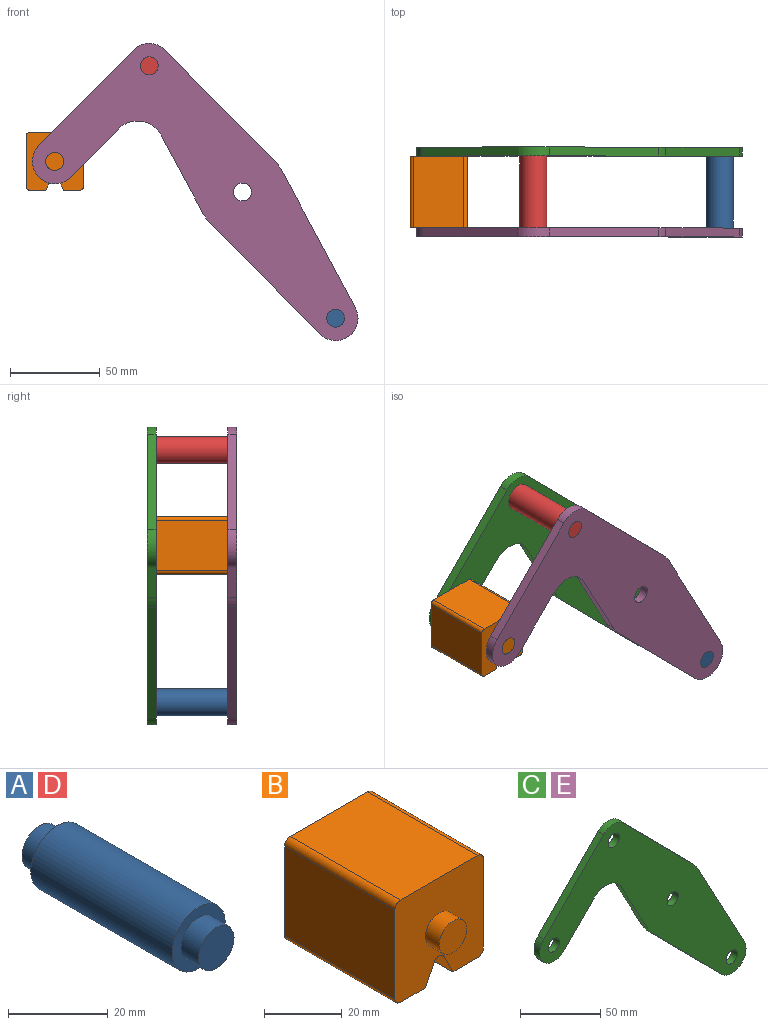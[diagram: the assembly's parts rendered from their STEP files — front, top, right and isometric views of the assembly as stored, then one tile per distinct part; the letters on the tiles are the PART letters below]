
ASSEMBLY  parts=5 mates=3
PART A: 7 faces, bbox 15x50x15 mm
  f0: cylinder r=7.5mm len=40mm, axis (0,-1,0), area 1885mm2, adj f2,f5
  f1: cylinder r=5mm len=10mm, axis (0,1,0), area 157.1mm2, adj f2,f3
  f2: plane 15x15mm, normal (0,-1,0), area 98.2mm2, adj f0,f1
  f3: plane 10x10mm, normal (0,-1,0), area 78.5mm2, adj f1
  f4: cylinder r=5mm len=10mm, axis (0,-1,0), area 157.1mm2, adj f5,f6
  f5: plane 15x15mm, normal (0,1,0), area 98.2mm2, adj f0,f4
  f6: plane 10x10mm, normal (0,1,0), area 78.5mm2, adj f4
PART B: 18 faces, bbox 32.1x50x32.1 mm
  f0: plane 40x28.08mm, normal (1,0,0), area 1123.1mm2, adj f4,f10,f13,f14
  f1: plane 40x9.04mm, normal (0,0,-1), area 361.6mm2, adj f2,f4,f10,f14
  f2: plane 40x6.42mm, normal (-0.89,0,-0.45), area 287.2mm2, adj f1,f4,f10,f15
  f3: plane 40x6.42mm, normal (0.89,0,-0.45), area 287.2mm2, adj f4,f5,f10,f15
  f4: plane 32.08x32.08mm, normal (0,-1,0), area 900.6mm2, adj f0,f1,f2,f3,f5,f6,f7,f9
  f5: plane 40x9.04mm, normal (0,0,-1), area 361.6mm2, adj f3,f4,f10,f16
  f6: plane 40x28.08mm, normal (0,0,1), area 1123.1mm2, adj f4,f10,f13,f17
  f7: plane 40x28.08mm, normal (-1,0,0), area 1123.1mm2, adj f4,f10,f16,f17
  f8: plane 10x10mm, normal (0,-1,0), area 78.5mm2, adj f9
  f9: cylinder r=5mm len=10mm, axis (0,1,0), area 157.1mm2, adj f4,f8
  f10: plane 32.08x32.08mm, normal (0,1,0), area 900.6mm2, adj f0,f1,f2,f3,f5,f6,f7,f12
  f11: plane 10x10mm, normal (0,1,0), area 78.5mm2, adj f12
  f12: cylinder r=5mm len=10mm, axis (0,-1,0), area 157.1mm2, adj f10,f11
  f13: cylinder r=2mm len=40mm, axis (0,1,0), area 125.7mm2, adj f0,f4,f6,f10
  f14: cylinder r=2mm len=40mm, axis (0,-1,0), area 125.7mm2, adj f0,f1,f4,f10
  f15: cylinder r=2mm len=40mm, axis (0,1,0), area 177.1mm2, adj f2,f3,f4,f10
  f16: cylinder r=2mm len=40mm, axis (0,1,0), area 125.7mm2, adj f4,f5,f7,f10
  f17: cylinder r=2mm len=40mm, axis (0,-1,0), area 125.7mm2, adj f4,f6,f7,f10
PART C: 18 faces, bbox 181.7x5x165.8 mm
  f0: plane 43.49x23.35mm, normal (-0.88,0,-0.47), area 246.8mm2, adj f1,f14,f16,f17
  f1: cylinder r=25mm len=5.75mm, axis (0,1,0), area 35.8mm2, adj f0,f2,f16,f17
  f2: plane 61.6x60.87mm, normal (-0.71,0,-0.7), area 433mm2, adj f1,f3,f16,f17
  f3: cylinder r=12.5mm len=21.39mm, axis (0,1,0), area 178.4mm2, adj f2,f4,f16,f17
  f4: plane 76.3x40.96mm, normal (0.88,0,0.47), area 433mm2, adj f3,f5,f16,f17
  f5: cylinder r=25mm len=5.75mm, axis (0,1,0), area 35.8mm2, adj f4,f6,f16,f17
  f6: plane 61.6x60.87mm, normal (0.71,0,0.7), area 433mm2, adj f5,f7,f16,f17
  f7: cylinder r=12.5mm len=17.78mm, axis (0,1,0), area 98.9mm2, adj f6,f8,f16,f17
  f8: plane 53.35x52.71mm, normal (-0.71,0,0.7), area 375mm2, adj f7,f9,f16,f17
  f9: cylinder r=12.5mm len=21.39mm, axis (0,1,0), area 196.3mm2, adj f8,f10,f16,f17
  f10: plane 26.86x26.54mm, normal (0.71,0,-0.7), area 188.8mm2, adj f9,f14,f16,f17
  f11: cylinder r=5mm len=10mm, axis (0,1,0), area 157.1mm2, adj f16,f17
  f12: cylinder r=5mm len=10mm, axis (0,1,0), area 157.1mm2, adj f16,f17
  f13: cylinder r=5mm len=10mm, axis (0,1,0), area 157.1mm2, adj f16,f17
  f14: cylinder r=15mm len=23.89mm, axis (0,1,0), area 140.2mm2, adj f0,f10,f16,f17
  f15: cylinder r=5mm len=10mm, axis (0,1,0), area 157.1mm2, adj f16,f17
  f16: plane 181.66x165.78mm, normal (0,-1,0), area 8710.1mm2, adj f0,f1,f2,f3,f4,f5,f6,f7
  f17: plane 181.66x165.78mm, normal (0,1,0), area 8710.1mm2, adj f0,f1,f2,f3,f4,f5,f6,f7
PART D: same geometry as A
PART E: same geometry as C
PLACE A t=(103.95,-20,-140.78)mm
PLACE B t=(0,-20,0)mm
PLACE C t=(0,25,0)mm
PLACE D t=(0,-20,0)mm
PLACE E t=(0,-20,0)mm fixed
MATE revolute E.f9 <-> B.f9  axis (0,1,0) through (-104.69,-20,17.04)mm
MATE fastened C.f7 <-> D.f0  axis (0,-1,0) through (-51.98,20,70.39)mm
MATE fastened A.f0 <-> E.f3  axis (0,1,0) through (51.98,-20,-70.39)mm
